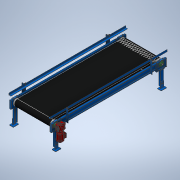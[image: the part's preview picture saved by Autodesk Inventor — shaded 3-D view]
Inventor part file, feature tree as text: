
AUTODESK INVENTOR PART (.ipt)
format: ipt  version: 2021 (Build 250183000, 183)  size: 5,187,584 bytes
history: native  units: mm
features: other x180, boolean_combine x1, shell x1
ambient origin geometry x8: Origin, YZ Plane, XZ Plane, XY Plane, X Axis, Y Axis, Z Axis, Center Point
bodies: Solid1 (feature_tree), Solid2 (feature_tree), Solid3 (feature_tree), Solid4 (feature_tree), Solid6 (feature_tree), Solid20 (feature_tree), Solid22 (feature_tree), Solid24 (feature_tree), Solid27 (feature_tree), Solid28 (feature_tree), Solid29 (feature_tree), Solid30 (feature_tree), Solid31 (feature_tree), Solid32 (feature_tree), Solid34 (feature_tree), Solid36 (feature_tree), Solid38 (feature_tree), Solid40 (feature_tree), Solid42 (feature_tree), Solid44 (feature_tree), Solid45 (feature_tree), Solid46 (feature_tree), Solid47 (feature_tree), Solid48 (feature_tree), Solid169 (feature_tree), Solid170 (feature_tree), Solid171 (feature_tree), Solid172 (feature_tree), Solid173 (feature_tree), Solid179 (feature_tree), Solid180 (feature_tree), Solid181 (feature_tree), Solid187 (feature_tree), Solid188 (feature_tree), Solid189 (feature_tree), Solid190 (feature_tree), Solid191 (feature_tree), Solid192 (feature_tree), Solid202 (feature_tree), Solid204 (feature_tree), Solid206 (feature_tree), Solid208 (feature_tree), Solid210 (feature_tree), Solid212 (feature_tree), Solid213 (feature_tree), Solid214 (feature_tree), Solid215 (feature_tree), Solid216 (feature_tree), Solid313 (feature_tree), Solid314 (feature_tree), Solid315 (feature_tree), Solid316 (feature_tree), Solid317 (feature_tree), Solid318 (feature_tree), Solid319 (feature_tree), Solid320 (feature_tree), Solid450 (feature_tree), Solid451 (feature_tree), Solid452 (feature_tree), Solid453 (feature_tree), Solid454 (feature_tree), Solid455 (feature_tree), Solid456 (feature_tree), Solid457 (feature_tree), Solid458 (feature_tree), Solid459 (feature_tree), Solid460 (feature_tree), Solid461 (feature_tree), Solid462 (feature_tree), Solid463 (feature_tree), Solid464 (feature_tree), Solid465 (feature_tree), Solid466 (feature_tree), Solid467 (feature_tree), Solid468 (feature_tree), Solid469 (feature_tree), Solid470 (feature_tree), Solid471 (feature_tree), Solid472 (feature_tree), Solid473 (feature_tree), Solid474 (feature_tree), Solid475 (feature_tree), Solid476 (feature_tree), Solid477 (feature_tree), Solid478 (feature_tree), Solid479 (feature_tree), Solid480 (feature_tree), Solid481 (feature_tree), Solid581 (feature_tree), Solid582 (feature_tree), Solid583 (feature_tree), Solid584 (feature_tree), Solid585 (feature_tree), Solid586 (feature_tree), Solid587 (feature_tree), Solid588 (feature_tree), Solid589 (feature_tree), Solid590 (feature_tree), Solid591 (feature_tree), Solid592 (feature_tree), Solid593 (feature_tree), Solid594 (feature_tree), Solid595 (feature_tree), Solid596 (feature_tree)
feature tree (182):
  other  "Flat Belt.iam"
  other  "Side Cover.ipt:1"
  other  "Guide.iam:1::L-Shape Guide.ipt:1"
  other  "Guide.iam:1::Support of Guide.ipt:1"
  other  "Guide.iam:1::Spacer of Guide.ipt:1"
  other  "Guide.iam:1::Spacer of Guide.ipt:2"
  other  "Guide.iam:1::Spacer of Guide.ipt:4"
  other  "Guide.iam:1::Spacer of Guide.ipt:6"
  other  "Guide.iam:1::Support of Guide.ipt:3"
  other  "Guide.iam:1::Alen Screw - M8x30.ipt:1"
  other  "Guide.iam:1::Spring Washer - A8.ipt:7"
  other  "Guide.iam:1::Spring Washer - A8.ipt:8"
  other  "Guide.iam:1::Alen Screw - M8x30.ipt:2"
  other  "Guide.iam:1::Hex Nut - M8.ipt:1"
  other  "Guide.iam:1::Hex Nut - M8.ipt:2"
  other  "Guide.iam:1::Alen Screw - M8x30.ipt:4"
  other  "Guide.iam:1::Spring Washer - A8.ipt:10"
  other  "Guide.iam:1::Spring Washer - A8.ipt:12"
  other  "Guide.iam:1::Alen Screw - M8x30.ipt:6"
  other  "Guide.iam:1::Hex Nut - M8.ipt:4"
  other  "Guide.iam:1::Hex Nut - M8.ipt:6"
  other  "Bracket.ipt:1"
  other  "Bracket.ipt:2"
  other  "Leg.ipt:1"
  other  "Bearing Guide.iam:1::Deep groove ball bearings - SKF 6304-2Z.ipt:1"
  other  "Bearing Guide.iam:1::Deep groove ball bearings - SKF 6304-2Z.ipt:2"
  other  "Bearing Guide.iam:1::Hex-Head Bolt - M8 x 100.ipt:1"
  other  "Bearing Guide.iam:1::Hex Nut - M8.ipt:1"
  other  "Bearing Guide.iam:2::Deep groove ball bearings - SKF 6304-2Z.ipt:1"
  other  "Bearing Guide.iam:2::Deep groove ball bearings - SKF 6304-2Z.ipt:2"
  other  "Bearing Guide.iam:2::Hex-Head Bolt - M8 x 100.ipt:1"
  other  "Bearing Guide.iam:2::Hex Nut - M8.ipt:1"
  other  "Bearing Guide.iam:3::Deep groove ball bearings - SKF 6304-2Z.ipt:1"
  other  "Bearing Guide.iam:3::Deep groove ball bearings - SKF 6304-2Z.ipt:2"
  other  "Bearing Guide.iam:3::Hex-Head Bolt - M8 x 100.ipt:1"
  other  "Bearing Guide.iam:3::Hex Nut - M8.ipt:1"
  other  "Bearing Guide.iam:4::Deep groove ball bearings - SKF 6304-2Z.ipt:1"
  other  "Bearing Guide.iam:4::Deep groove ball bearings - SKF 6304-2Z.ipt:2"
  other  "Bearing Guide.iam:4::Hex-Head Bolt - M8 x 100.ipt:1"
  other  "Bearing Guide.iam:4::Hex Nut - M8.ipt:1"
  other  "Bearing Guide.iam:5::Deep groove ball bearings - SKF 6304-2Z.ipt:1"
  other  "Bearing Guide.iam:5::Deep groove ball bearings - SKF 6304-2Z.ipt:2"
  other  "Bearing Guide.iam:5::Hex-Head Bolt - M8 x 100.ipt:1"
  other  "Bearing Guide.iam:5::Hex Nut - M8.ipt:1"
  other  "Bearing Guide.iam:6::Deep groove ball bearings - SKF 6304-2Z.ipt:1"
  other  "Bearing Guide.iam:6::Deep groove ball bearings - SKF 6304-2Z.ipt:2"
  other  "Bearing Guide.iam:6::Hex-Head Bolt - M8 x 100.ipt:1"
  other  "Bearing Guide.iam:6::Hex Nut - M8.ipt:1"
  other  "Bearing Guide.iam:7::Deep groove ball bearings - SKF 6304-2Z.ipt:1"
  other  "Bearing Guide.iam:7::Deep groove ball bearings - SKF 6304-2Z.ipt:2"
  other  "Bearing Guide.iam:7::Hex-Head Bolt - M8 x 100.ipt:1"
  other  "Bearing Guide.iam:7::Hex Nut - M8.ipt:1"
  other  "Bearing Guide.iam:8::Deep groove ball bearings - SKF 6304-2Z.ipt:1"
  other  "Bearing Guide.iam:8::Deep groove ball bearings - SKF 6304-2Z.ipt:2"
  other  "Bearing Guide.iam:8::Hex-Head Bolt - M8 x 100.ipt:1"
  other  "Bearing Guide.iam:8::Hex Nut - M8.ipt:1"
  other  "Bearing Guide.iam:9::Deep groove ball bearings - SKF 6304-2Z.ipt:1"
  other  "Bearing Guide.iam:9::Deep groove ball bearings - SKF 6304-2Z.ipt:2"
  other  "Bearing Guide.iam:9::Hex-Head Bolt - M8 x 100.ipt:1"
  other  "Bearing Guide.iam:9::Hex Nut - M8.ipt:1"
  other  "Bearing Guide.iam:10::Deep groove ball bearings - SKF 6304-2Z.ipt:1"
  other  "Bearing Guide.iam:10::Deep groove ball bearings - SKF 6304-2Z.ipt:2"
  other  "Bearing Guide.iam:10::Hex-Head Bolt - M8 x 100.ipt:1"
  other  "Bearing Guide.iam:10::Hex Nut - M8.ipt:1"
  other  "Bearing Guide.iam:11::Deep groove ball bearings - SKF 6304-2Z.ipt:1"
  other  "Bearing Guide.iam:11::Deep groove ball bearings - SKF 6304-2Z.ipt:2"
  other  "Bearing Guide.iam:11::Hex-Head Bolt - M8 x 100.ipt:1"
  other  "Bearing Guide.iam:11::Hex Nut - M8.ipt:1"
  other  "Bearing Guide.iam:12::Deep groove ball bearings - SKF 6304-2Z.ipt:1"
  other  "Bearing Guide.iam:12::Deep groove ball bearings - SKF 6304-2Z.ipt:2"
  other  "Bearing Guide.iam:12::Hex-Head Bolt - M8 x 100.ipt:1"
  other  "Bearing Guide.iam:12::Hex Nut - M8.ipt:1"
  other  "Side Cover_MIR.ipt:1"
  other  "Guide_MIR.iam:1::L-Shape Guide_MIR.ipt:1"
  other  "Guide_MIR.iam:1::Support of Guide_MIR.ipt:1"
  other  "Guide_MIR.iam:1::Spacer of Guide_MIR.ipt:1"
  other  "Guide_MIR.iam:1::Spacer of Guide_MIR.ipt:2"
  other  "Guide_MIR.iam:1::Support of Guide_MIR.ipt:4"
  other  "Guide_MIR.iam:1::Spacer of Guide_MIR.ipt:7"
  other  "Guide_MIR.iam:1::Spacer of Guide_MIR.ipt:8"
  other  "Guide_MIR.iam:1::Spring Washer - A8.ipt:3"
  other  "Guide_MIR.iam:1::Spring Washer - A8.ipt:4"
  other  "Guide_MIR.iam:1::Alen Screw - M8x30.ipt:1"
  other  "Guide_MIR.iam:1::Alen Screw - M8x30.ipt:2"
  other  "Guide_MIR.iam:1::Hex Nut - M8.ipt:1"
  other  "Guide_MIR.iam:1::Hex Nut - M8.ipt:2"
  other  "Guide_MIR.iam:1::Spring Washer - A8.ipt:10"
  other  "Guide_MIR.iam:1::Spring Washer - A8.ipt:12"
  other  "Guide_MIR.iam:1::Alen Screw - M8x30.ipt:4"
  other  "Guide_MIR.iam:1::Alen Screw - M8x30.ipt:6"
  other  "Guide_MIR.iam:1::Hex Nut - M8.ipt:4"
  other  "Guide_MIR.iam:1::Hex Nut - M8.ipt:6"
  other  "UCF207.ipt:1"
  other  "UCF207.ipt:2"
  other  "UCF207.ipt:3"
  other  "UCF207.ipt:4"
  other  "PVC-3.ipt:1"
  other  "_SAZ47DRS71M4idut3juhqgwvy5qynxepxibh_AP214.ipt:1"
  other  "Roll 160.ipt:1"
  other  "Roll 160.ipt:2"
  other  "Bearing Guide.iam:13::Deep groove ball bearings - SKF 6304-2Z.ipt:1"
  other  "Bearing Guide.iam:13::Deep groove ball bearings - SKF 6304-2Z.ipt:2"
  other  "Bearing Guide.iam:13::Hex-Head Bolt - M8 x 100.ipt:1"
  other  "Bearing Guide.iam:13::Hex Nut - M8.ipt:1"
  other  "Bearing Guide.iam:14::Deep groove ball bearings - SKF 6304-2Z.ipt:1"
  other  "Bearing Guide.iam:14::Deep groove ball bearings - SKF 6304-2Z.ipt:2"
  other  "Bearing Guide.iam:14::Hex-Head Bolt - M8 x 100.ipt:1"
  other  "Bearing Guide.iam:14::Hex Nut - M8.ipt:1"
  other  "Bearing Guide.iam:15::Deep groove ball bearings - SKF 6304-2Z.ipt:1"
  other  "Bearing Guide.iam:15::Deep groove ball bearings - SKF 6304-2Z.ipt:2"
  other  "Bearing Guide.iam:15::Hex-Head Bolt - M8 x 100.ipt:1"
  other  "Bearing Guide.iam:15::Hex Nut - M8.ipt:1"
  other  "Bearing Guide.iam:16::Deep groove ball bearings - SKF 6304-2Z.ipt:1"
  other  "Bearing Guide.iam:16::Deep groove ball bearings - SKF 6304-2Z.ipt:2"
  other  "Bearing Guide.iam:16::Hex-Head Bolt - M8 x 100.ipt:1"
  other  "Bearing Guide.iam:16::Hex Nut - M8.ipt:1"
  other  "Bearing Guide.iam:17::Deep groove ball bearings - SKF 6304-2Z.ipt:1"
  other  "Bearing Guide.iam:17::Deep groove ball bearings - SKF 6304-2Z.ipt:2"
  other  "Bearing Guide.iam:17::Hex-Head Bolt - M8 x 100.ipt:1"
  other  "Bearing Guide.iam:17::Hex Nut - M8.ipt:1"
  other  "Bearing Guide.iam:18::Deep groove ball bearings - SKF 6304-2Z.ipt:1"
  other  "Bearing Guide.iam:18::Deep groove ball bearings - SKF 6304-2Z.ipt:2"
  other  "Bearing Guide.iam:18::Hex-Head Bolt - M8 x 100.ipt:1"
  other  "Bearing Guide.iam:18::Hex Nut - M8.ipt:1"
  other  "Bearing Guide.iam:19::Deep groove ball bearings - SKF 6304-2Z.ipt:1"
  other  "Bearing Guide.iam:19::Deep groove ball bearings - SKF 6304-2Z.ipt:2"
  other  "Bearing Guide.iam:19::Hex-Head Bolt - M8 x 100.ipt:1"
  other  "Bearing Guide.iam:19::Hex Nut - M8.ipt:1"
  other  "Bearing Guide.iam:20::Deep groove ball bearings - SKF 6304-2Z.ipt:1"
  other  "Bearing Guide.iam:20::Deep groove ball bearings - SKF 6304-2Z.ipt:2"
  other  "Bearing Guide.iam:20::Hex-Head Bolt - M8 x 100.ipt:1"
  other  "Bearing Guide.iam:20::Hex Nut - M8.ipt:1"
  other  "Alen Screw - M12x30.ipt:1"
  other  "Alen Screw - M12x30.ipt:2"
  other  "Alen Screw - M12x30.ipt:3"
  other  "Alen Screw - M12x30.ipt:4"
  other  "Alen Screw - M12x30.ipt:5"
  other  "Alen Screw - M12x30.ipt:6"
  other  "Alen Screw - M12x30.ipt:7"
  other  "Alen Screw - M12x30.ipt:8"
  other  "Alen Screw - M10x20.ipt:1"
  other  "Alen Screw - M10x20.ipt:2"
  other  "Alen Screw - M10x20.ipt:3"
  other  "Alen Screw - M10x20.ipt:4"
  other  "Plain washers for bolts with heavy clamping sleeves - 10.5.ipt:1"
  other  "Plain washers for bolts with heavy clamping sleeves - 10.5.ipt:2"
  other  "Plain washers for bolts with heavy clamping sleeves - 10.5.ipt:3"
  other  "Plain washers for bolts with heavy clamping sleeves - 10.5.ipt:4"
  other  "Alen Screw - M12x30.ipt:9"
  other  "Alen Screw - M12x30.ipt:10"
  other  "Alen Screw - M12x30.ipt:11"
  other  "Alen Screw - M12x30.ipt:12"
  other  "Alen Screw - M12x30.ipt:13"
  other  "Alen Screw - M12x30.ipt:14"
  other  "Alen Screw - M12x30.ipt:15"
  other  "Alen Screw - M12x30.ipt:16"
  other  "Alen Screw - M10x20.ipt:5"
  other  "Alen Screw - M10x20.ipt:6"
  other  "Alen Screw - M10x20.ipt:7"
  other  "Alen Screw - M10x20.ipt:8"
  other  "Plain washers for bolts with heavy clamping sleeves - 10.5.ipt:5"
  other  "Plain washers for bolts with heavy clamping sleeves - 10.5.ipt:6"
  other  "Plain washers for bolts with heavy clamping sleeves - 10.5.ipt:7"
  other  "Plain washers for bolts with heavy clamping sleeves - 10.5.ipt:8"
  other  "Spring Washer - A8.ipt:1"
  other  "Spring Washer - A8.ipt:2"
  other  "Spring Washer - A8.ipt:3"
  other  "Spring Washer - A8.ipt:4"
  other  "Alen Screw - M8x25.ipt:1"
  other  "Alen Screw - M8x25.ipt:2"
  other  "Alen Screw - M8x25.ipt:3"
  other  "Alen Screw - M8x25.ipt:4"
  other  "Spring Washer - A8.ipt:5"
  other  "Spring Washer - A8.ipt:6"
  other  "Spring Washer - A8.ipt:7"
  other  "Spring Washer - A8.ipt:8"
  other  "Alen Screw - M8x25.ipt:5"
  other  "Alen Screw - M8x25.ipt:6"
  other  "Alen Screw - M8x25.ipt:7"
  other  "Alen Screw - M8x25.ipt:8"
  boolean_combine  "Combine1"
  shell  "Shell1"  Thickness=10.0mm
